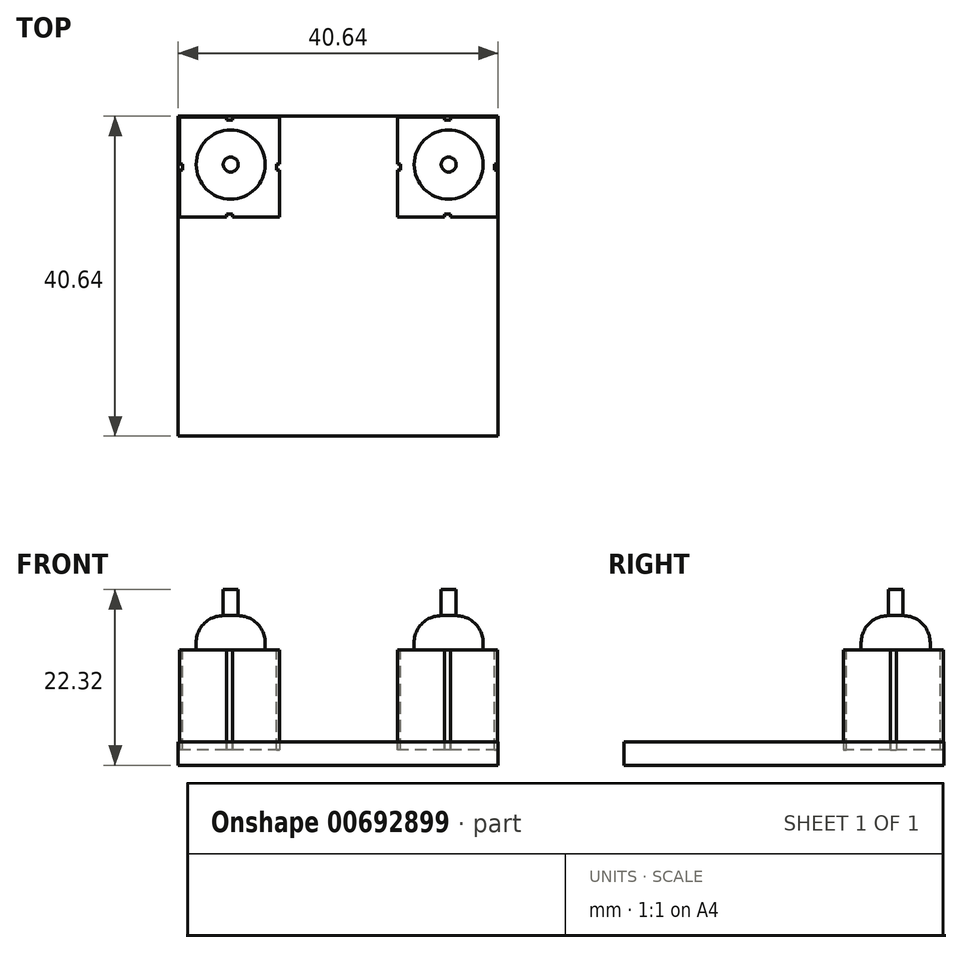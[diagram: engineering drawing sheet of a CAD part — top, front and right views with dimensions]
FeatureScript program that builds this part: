
annotation { "Feature Type Name" : "Feature", "Feature Type Description" : "" }
export const myFeature = defineFeature(function(context is Context, id is Id, definition is map)
    precondition{}
    {
        {
            var Q0;
            Q0=qCreatedBy(makeId("Top.planeOp"),FACE);
            var sketch = newSketch(context, id + "F0", { "sketchPlane" : qUnion([Q0])});
            skLineSegment(sketch, "E0.bottom", {"start": v(-40.64, 35.15) * mm, "end": v(0, 35.15) * mm});
            skLineSegment(sketch, "E0.top", {"start": v(-40.64, -5.49) * mm, "end": v(0, -5.49) * mm});
            skLineSegment(sketch, "E0.left", {"start": v(-40.64, 35.15) * mm, "end": v(-40.64, -5.49) * mm});
            skLineSegment(sketch, "E0.right", {"start": v(0, 35.15) * mm, "end": v(0, -5.49) * mm});
            skSolve(sketch);
        }
        {
            var Q0;
            Q0=makeQuery(id+"F0.imprint","IMPRINT",FACE,{"disambiguationData":[TD([[makeQuery(id+"F0.imprint","IMPRINT",EDGE,{"derivedFrom":sQuery(id+"F0.wireOp",EDGE,"E0.bottom")}),-1.0]])]});
            extrude(context, id + "F1", {"entities" : qUnion([Q0]), "depth" : 3 * mm, "offsetDistance" : 25.4 * mm});
        }
        {
            var Q0;
            Q0=qCreatedBy(makeId("Front.planeOp"),FACE);
            var sketch = newSketch(context, id + "F2", { "sketchPlane" : qUnion([Q0])});
            skLineSegment(sketch, "E1.bottom", {"start": v(12.03, 31.4) * mm, "end": v(24.73, 31.4) * mm});
            skLineSegment(sketch, "E1.top", {"start": v(12.03, 18.7) * mm, "end": v(24.73, 18.7) * mm});
            skLineSegment(sketch, "E1.left", {"start": v(12.03, 31.4) * mm, "end": v(12.03, 18.7) * mm});
            skLineSegment(sketch, "E1.right", {"start": v(24.73, 31.4) * mm, "end": v(24.73, 18.7) * mm});
            skSolve(sketch);
        }
        {
            var Q0;
            Q0=makeQuery(id+"F2.imprint","IMPRINT",FACE,{"disambiguationData":[TD([[makeQuery(id+"F2.imprint","IMPRINT",EDGE,{"derivedFrom":sQuery(id+"F2.wireOp",EDGE,"E1.bottom")}),-1.0]])]});
            extrude(context, id + "F3", {"entities" : qUnion([Q0]), "depth" : 12.7 * mm, "offsetDistance" : 25.4 * mm});
        }
        {
            var Q0;
            Q0=makeQuery(id+"F3.opExtrude","SWEPT_BODY",BODY,{"disambiguationData":[OSD([sQuery(id+"F2.wireOp",EDGE,"E1.bottom"),sQuery(id+"F2.wireOp",EDGE,"E1.top"),sQuery(id+"F2.wireOp",EDGE,"E1.left"),sQuery(id+"F2.wireOp",EDGE,"E1.right")])]});
            transform(context, id + "F4", {"entities" : qUnion([Q0]), "transformType" : TransformType.TRANSLATION_3D, "dx" : -18.38 * mm, "dy" : 0 * mm, "dz" : 0 * mm, "makeCopy" : false});
        }
        {
            var Q0;
            Q0=qCreatedBy(makeId("Front.planeOp"),FACE);
            var sketch = newSketch(context, id + "F5", { "sketchPlane" : qUnion([Q0])});
            skLineSegment(sketch, "E2", {"start": v(0, 31.03) * mm, "end": v(-0.38, 31.03) * mm});
            skLineSegment(sketch, "E3", {"start": v(-0.38, 31.03) * mm, "end": v(-0.38, 31.48) * mm});
            skLineSegment(sketch, "E4", {"start": v(0, 19.1) * mm, "end": v(-0.38, 19.1) * mm});
            skLineSegment(sketch, "E5", {"start": v(-0.38, 19.1) * mm, "end": v(-0.38, 18.63) * mm});
            skLineSegment(sketch, "E6.MirrorCS", {"start": v(0, 19.1) * mm, "end": v(0.38, 19.1) * mm});
            skLineSegment(sketch, "E7.MirrorCS", {"start": v(0.38, 19.1) * mm, "end": v(0.38, 18.63) * mm});
            skLineSegment(sketch, "E8.MirrorCS", {"start": v(0, 31.03) * mm, "end": v(0.38, 31.03) * mm});
            skLineSegment(sketch, "E9.MirrorCS", {"start": v(0.38, 31.03) * mm, "end": v(0.38, 31.48) * mm});
            skLineSegment(sketch, "E10", {"start": v(-0.38, 31.48) * mm, "end": v(0.38, 31.48) * mm});
            skLineSegment(sketch, "E11", {"start": v(-0.38, 18.63) * mm, "end": v(0.38, 18.63) * mm});
            skLineSegment(sketch, "E12.bottom", {"start": v(-6.45, 25.44) * mm, "end": v(-5.97, 25.44) * mm});
            skLineSegment(sketch, "E12.top", {"start": v(-6.45, 24.68) * mm, "end": v(-5.97, 24.68) * mm});
            skLineSegment(sketch, "E12.left", {"start": v(-6.45, 25.44) * mm, "end": v(-6.45, 24.68) * mm});
            skLineSegment(sketch, "E12.right", {"start": v(-5.97, 25.44) * mm, "end": v(-5.97, 24.68) * mm});
            skLineSegment(sketch, "E13.MirrorCS", {"start": v(5.97, 25.44) * mm, "end": v(5.97, 24.68) * mm});
            skLineSegment(sketch, "E14.MirrorCS", {"start": v(6.45, 25.44) * mm, "end": v(6.45, 24.68) * mm});
            skLineSegment(sketch, "E15.MirrorCS", {"start": v(6.45, 25.44) * mm, "end": v(5.97, 25.44) * mm});
            skLineSegment(sketch, "E16.MirrorCS", {"start": v(6.45, 24.68) * mm, "end": v(5.97, 24.68) * mm});
            skSolve(sketch);
        }
        {
            var Q0;
            Q0=makeQuery(id+"F5.imprint","IMPRINT",FACE,{"disambiguationData":[TD([[makeQuery(id+"F5.imprint","IMPRINT",EDGE,{"derivedFrom":sQuery(id+"F5.wireOp",EDGE,"E2")}),-1.0]])]});
            var Q1;
            Q1=makeQuery(id+"F5.imprint","IMPRINT",FACE,{"disambiguationData":[TD([[makeQuery(id+"F5.imprint","IMPRINT",EDGE,{"derivedFrom":sQuery(id+"F5.wireOp",EDGE,"E4")}),1.0]])]});
            var Q2;
            Q2=makeQuery(id+"F5.imprint","IMPRINT",FACE,{"disambiguationData":[TD([[makeQuery(id+"F5.imprint","IMPRINT",EDGE,{"derivedFrom":sQuery(id+"F5.wireOp",EDGE,"E12.bottom")}),-1.0]])]});
            var Q3;
            Q3=makeQuery(id+"F5.imprint","IMPRINT",FACE,{"disambiguationData":[TD([[makeQuery(id+"F5.imprint","IMPRINT",EDGE,{"derivedFrom":sQuery(id+"F5.wireOp",EDGE,"E13.MirrorCS")}),1.0]])]});
            extrude(context, id + "F6", {"entities" : qUnion([Q0, Q1, Q2, Q3]), "operationType" : NewBodyOperationType.REMOVE, "endBound" : BoundingType.SYMMETRIC, "oppositeDirection" : true, "depth" : 25.4 * mm, "offsetDistance" : 25.4 * mm});
        }
        {
            var Q0;
            Q0=makeQuery(id+"F3.opExtrude","SWEPT_BODY",BODY,{"disambiguationData":[OSD([sQuery(id+"F2.wireOp",EDGE,"E1.bottom"),sQuery(id+"F2.wireOp",EDGE,"E1.top"),sQuery(id+"F2.wireOp",EDGE,"E1.left"),sQuery(id+"F2.wireOp",EDGE,"E1.right")])]});
            var Q1;
            Q1=makeQuery(id+"F3.opExtrude","SWEPT_EDGE",EDGE,{"disambiguationData":[OSD([sQuery(id+"F2.wireOp",EDGE,"E1.top"),sQuery(id+"F2.wireOp",EDGE,"E1.right")])]});
            transform(context, id + "F7", {"entities" : qUnion([Q0]), "transformType" : TransformType.ROTATION, "transformAxis" : qUnion([Q1]), "angle" : 90 * degree, "makeCopy" : false});
        }
        {
            var Q0;
            Q0=makeQuery(id+"F3.opExtrude","SWEPT_BODY",BODY,{"disambiguationData":[OSD([sQuery(id+"F2.wireOp",EDGE,"E1.bottom"),sQuery(id+"F2.wireOp",EDGE,"E1.top"),sQuery(id+"F2.wireOp",EDGE,"E1.left"),sQuery(id+"F2.wireOp",EDGE,"E1.right")])]});
            transform(context, id + "F8", {"entities" : qUnion([Q0]), "transformType" : TransformType.TRANSLATION_3D, "dx" : -12.7 * mm, "dy" : 0 * mm, "dz" : 0 * mm, "makeCopy" : false});
        }
        {
            var Q0;
            Q0=makeQuery(id+"F3.opExtrude","SWEPT_BODY",BODY,{"disambiguationData":[OSD([sQuery(id+"F2.wireOp",EDGE,"E1.bottom"),sQuery(id+"F2.wireOp",EDGE,"E1.top"),sQuery(id+"F2.wireOp",EDGE,"E1.left"),sQuery(id+"F2.wireOp",EDGE,"E1.right")])]});
            var Q1;
            {var subQ0=sQuery(id+"F2.wireOp",EDGE,"E1.right");var subQ1=sQuery(id+"F2.wireOp",EDGE,"E1.top");Q1=makeQuery(id+"F6.boolean.opBoolean","SPLIT",EDGE,{"disambiguationData":[TD([makeQuery(id+"F3.opExtrude","SWEPT_FACE",FACE,{"disambiguationData":[OSD([subQ1])]})])],"derivedFrom":makeQuery(id+"F3.opExtrude","CAP_EDGE",EDGE,{"disambiguationData":[OSD([subQ0])],"isStart":true})});}
            transform(context, id + "F9", {"entities" : qUnion([Q0]), "transformType" : TransformType.ROTATION, "transformAxis" : qUnion([Q1]), "angle" : 90 * degree, "makeCopy" : false});
        }
        {
            var Q0;
            Q0=makeQuery(id+"F3.opExtrude","SWEPT_BODY",BODY,{"disambiguationData":[OSD([sQuery(id+"F2.wireOp",EDGE,"E1.bottom"),sQuery(id+"F2.wireOp",EDGE,"E1.top"),sQuery(id+"F2.wireOp",EDGE,"E1.left"),sQuery(id+"F2.wireOp",EDGE,"E1.right")])]});
            transform(context, id + "F10", {"entities" : qUnion([Q0]), "transformType" : TransformType.TRANSLATION_3D, "dx" : -6.4 * mm, "dy" : 22.35 * mm, "dz" : -16.76 * mm, "makeCopy" : false});
        }
        {
            var Q0;
            Q0=makeQuery(id+"F3.opExtrude","CAP_FACE",FACE,{"disambiguationData":[OSD([sQuery(id+"F2.wireOp",EDGE,"E1.bottom"),sQuery(id+"F2.wireOp",EDGE,"E1.top"),sQuery(id+"F2.wireOp",EDGE,"E1.left"),sQuery(id+"F2.wireOp",EDGE,"E1.right")])],"isStart":false});
            var sketch = newSketch(context, id + "F11", { "sketchPlane" : qUnion([Q0])});
            skCircle(sketch, "E17", {"center": v(-6.28, 29.01) * mm, "radius": 4.38 * mm});
            skSolve(sketch);
        }
        {
            var Q0;
            Q0=makeQuery(id+"F11.imprint","IMPRINT",FACE,{"disambiguationData":[TD([[makeQuery(id+"F11.imprint","IMPRINT",EDGE,{"derivedFrom":sQuery(id+"F11.wireOp",EDGE,"E17")}),1.0]])]});
            extrude(context, id + "F12", {"entities" : qUnion([Q0]), "operationType" : NewBodyOperationType.ADD, "depth" : 4.37 * mm, "offsetDistance" : 25.4 * mm});
        }
        {
            var Q0;
            Q0=makeQuery(id+"F12.opExtrude","CAP_EDGE",EDGE,{"disambiguationData":[OSD([sQuery(id+"F11.wireOp",EDGE,"E17")])],"isStart":false});
            fillet(context, id + "F13", {"entities" : qUnion([Q0]), "radius" : 3.43 * mm, "tangentPropagation" : true, "allowEdgeOverflow" : false});
        }
        {
            var Q0;
            Q0=makeQuery(id+"F12.opExtrude","CAP_FACE",FACE,{"disambiguationData":[OSD([sQuery(id+"F11.wireOp",EDGE,"E17")])],"isStart":false});
            extrude(context, id + "F14", {"entities" : qUnion([Q0]), "operationType" : NewBodyOperationType.ADD, "depth" : 3.3 * mm, "offsetDistance" : 25.4 * mm});
        }
        {
            var Q0;
            Q0=makeQuery(id+"F3.opExtrude","SWEPT_BODY",BODY,{"disambiguationData":[OSD([sQuery(id+"F2.wireOp",EDGE,"E1.bottom"),sQuery(id+"F2.wireOp",EDGE,"E1.top"),sQuery(id+"F2.wireOp",EDGE,"E1.left"),sQuery(id+"F2.wireOp",EDGE,"E1.right")])]});
            transform(context, id + "F15", {"entities" : qUnion([Q0]), "transformType" : TransformType.TRANSLATION_3D, "dx" : -27.7 * mm, "dy" : 0 * mm, "dz" : 0 * mm, "makeCopy" : true});
        }
    });
